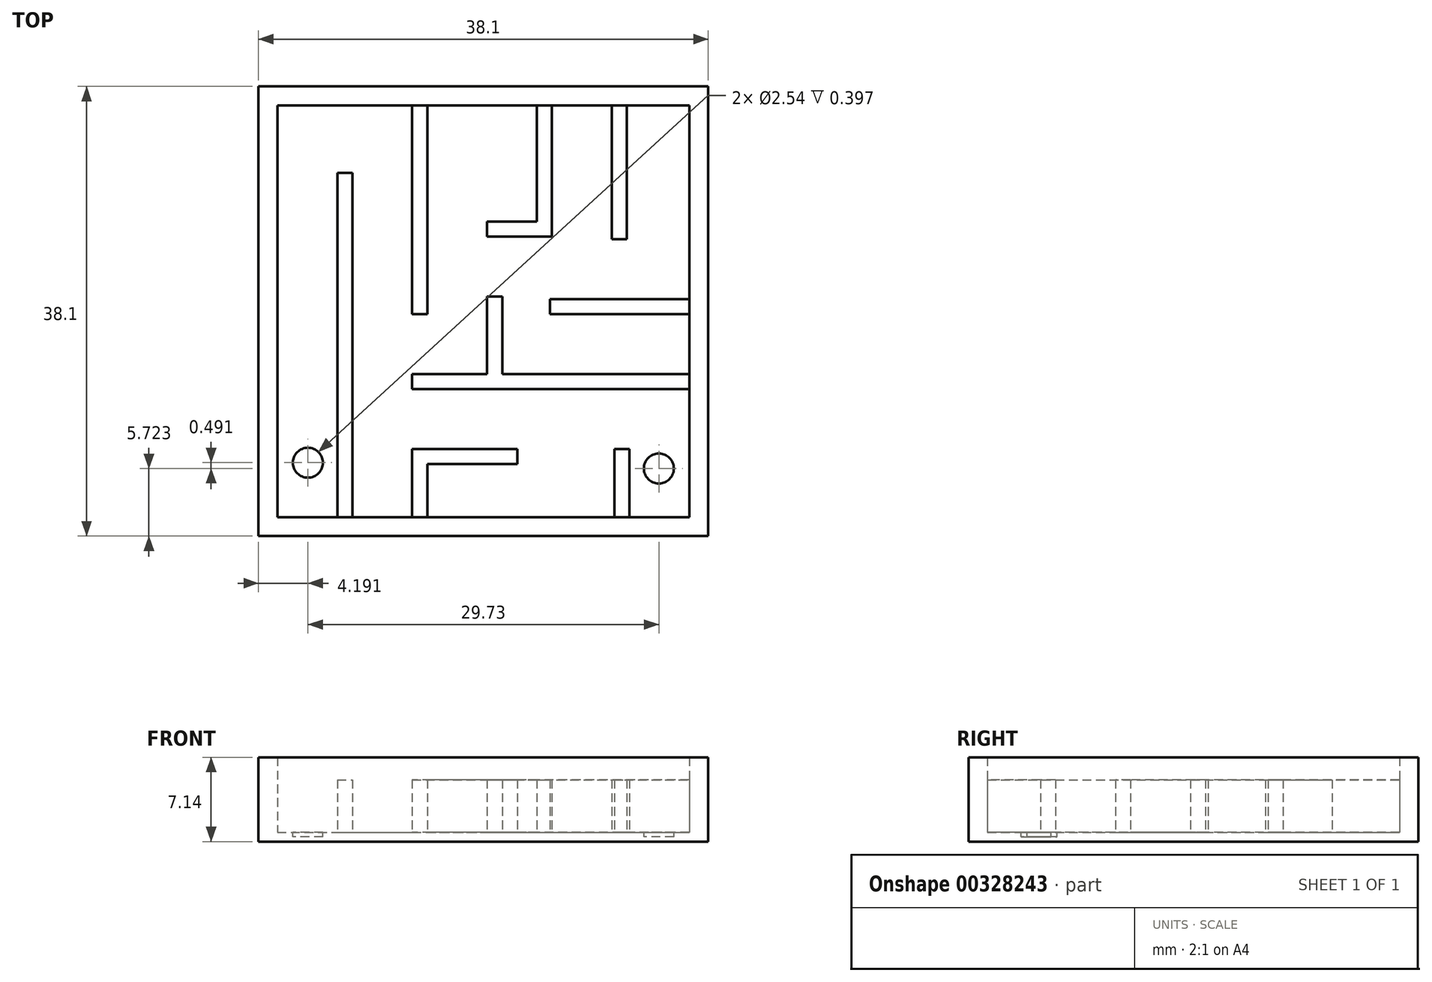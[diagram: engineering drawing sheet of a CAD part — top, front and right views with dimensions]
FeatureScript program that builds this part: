
annotation { "Feature Type Name" : "Feature", "Feature Type Description" : "" }
export const myFeature = defineFeature(function(context is Context, id is Id, definition is map)
    precondition{}
    {
        {
            var Q0;
            Q0=qCreatedBy(makeId("Top.planeOp"),FACE);
            var sketch = newSketch(context, id + "F0", { "sketchPlane" : qUnion([Q0])});
            skLineSegment(sketch, "E0.bottom", {"start": v(-16.83, 23.5) * mm, "end": v(21.27, 23.5) * mm});
            skLineSegment(sketch, "E0.top", {"start": v(-16.83, -14.6) * mm, "end": v(21.27, -14.6) * mm});
            skLineSegment(sketch, "E0.left", {"start": v(-16.83, 23.5) * mm, "end": v(-16.83, -14.6) * mm});
            skLineSegment(sketch, "E0.right", {"start": v(21.27, 23.5) * mm, "end": v(21.27, -14.6) * mm});
            skSolve(sketch);
        }
        {
            var Q0;
            Q0=makeQuery(id+"F0.imprint","IMPRINT",FACE,{"disambiguationData":[TD([[makeQuery(id+"F0.imprint","IMPRINT",EDGE,{"derivedFrom":sQuery(id+"F0.wireOp",EDGE,"E0.bottom")}),-1.0]])]});
            extrude(context, id + "F1", {"entities" : qUnion([Q0]), "depth" : 0.8 * mm});
        }
        {
            var Q0;
            Q0=makeQuery(id+"F1.opExtrude","CAP_FACE",FACE,{"disambiguationData":[OSD([sQuery(id+"F0.wireOp",EDGE,"E0.bottom"),sQuery(id+"F0.wireOp",EDGE,"E0.top"),sQuery(id+"F0.wireOp",EDGE,"E0.left"),sQuery(id+"F0.wireOp",EDGE,"E0.right")])],"isStart":false});
            var sketch = newSketch(context, id + "F2", { "sketchPlane" : qUnion([Q0])});
            skLineSegment(sketch, "E1.0", {"start": v(-15.23, 21.9) * mm, "end": v(19.67, 21.9) * mm});
            skLineSegment(sketch, "E1.1", {"start": v(-15.23, 21.9) * mm, "end": v(-15.23, -13) * mm});
            skLineSegment(sketch, "E1.2", {"start": v(-15.23, -13) * mm, "end": v(19.67, -13) * mm});
            skLineSegment(sketch, "E1.3", {"start": v(19.67, 21.9) * mm, "end": v(19.67, -13) * mm});
            skSolve(sketch);
        }
        {
            var Q0;
            Q0=makeQuery(id+"F2.imprint","IMPRINT",FACE,{"disambiguationData":[TD([[makeQuery(id+"F2.imprint","IMPRINT",EDGE,{"derivedFrom":sQuery(id+"F2.wireOp",EDGE,"E1.0")}),1.0]])]});
            extrude(context, id + "F3", {"entities" : qUnion([Q0]), "operationType" : NewBodyOperationType.ADD, "depth" : 6.35 * mm});
        }
        {
            var Q0;
            Q0=makeQuery(id+"F1.opExtrude","CAP_FACE",FACE,{"disambiguationData":[OSD([sQuery(id+"F0.wireOp",EDGE,"E0.bottom"),sQuery(id+"F0.wireOp",EDGE,"E0.top"),sQuery(id+"F0.wireOp",EDGE,"E0.left"),sQuery(id+"F0.wireOp",EDGE,"E0.right")])],"isStart":false});
            var sketch = newSketch(context, id + "F4", { "sketchPlane" : qUnion([Q0])});
            skLineSegment(sketch, "E2", {"start": v(-10.15, -13) * mm, "end": v(-10.15, 16.19) * mm});
            skLineSegment(sketch, "E3", {"start": v(-10.15, 16.19) * mm, "end": v(-8.88, 16.19) * mm});
            skLineSegment(sketch, "E4", {"start": v(-8.88, 16.19) * mm, "end": v(-8.88, -13) * mm});
            skLineSegment(sketch, "E5", {"start": v(-8.88, -13) * mm, "end": v(-10.15, -13) * mm});
            skLineSegment(sketch, "E6", {"start": v(-3.8, 21.9) * mm, "end": v(-3.8, 4.2) * mm});
            skLineSegment(sketch, "E7", {"start": v(-3.8, 4.2) * mm, "end": v(-2.53, 4.2) * mm});
            skLineSegment(sketch, "E8", {"start": v(-2.53, 4.2) * mm, "end": v(-2.53, 21.9) * mm});
            skLineSegment(sketch, "E9", {"start": v(-2.53, 21.9) * mm, "end": v(-3.8, 21.9) * mm});
            skLineSegment(sketch, "E10", {"start": v(-3.8, -0.88) * mm, "end": v(2.55, -0.88) * mm});
            skLineSegment(sketch, "E11", {"start": v(19.67, -0.88) * mm, "end": v(19.67, -2.15) * mm});
            skLineSegment(sketch, "E12", {"start": v(19.67, -2.15) * mm, "end": v(-3.8, -2.15) * mm});
            skLineSegment(sketch, "E13", {"start": v(-3.8, -2.15) * mm, "end": v(-3.8, -0.88) * mm});
            skLineSegment(sketch, "E14", {"start": v(19.67, 10.55) * mm, "end": v(19.67, 21.9) * mm});
            skLineSegment(sketch, "E15", {"start": v(19.67, 21.9) * mm, "end": v(2.55, 21.9) * mm});
            skLineSegment(sketch, "E16", {"start": v(2.55, -0.88) * mm, "end": v(2.55, 5.7) * mm});
            skLineSegment(sketch, "E17", {"start": v(2.55, 5.7) * mm, "end": v(3.82, 5.7) * mm});
            skLineSegment(sketch, "E18", {"start": v(3.82, 5.7) * mm, "end": v(3.82, -0.88) * mm});
            skLineSegment(sketch, "E19", {"start": v(-3.8, -13) * mm, "end": v(-3.8, -7.23) * mm});
            skLineSegment(sketch, "E20", {"start": v(-3.8, -7.23) * mm, "end": v(3.82, -7.23) * mm});
            skLineSegment(sketch, "E21", {"start": v(3.82, -7.23) * mm, "end": v(3.82, -7.23) * mm});
            skLineSegment(sketch, "E22", {"start": v(3.82, -7.23) * mm, "end": v(5.09, -7.23) * mm});
            skLineSegment(sketch, "E23", {"start": v(5.09, -7.23) * mm, "end": v(5.09, -8.5) * mm});
            skLineSegment(sketch, "E24", {"start": v(5.09, -8.5) * mm, "end": v(-2.53, -8.5) * mm});
            skLineSegment(sketch, "E25", {"start": v(-2.53, -8.5) * mm, "end": v(-2.53, -13) * mm});
            skLineSegment(sketch, "E26", {"start": v(-2.53, -13) * mm, "end": v(-3.8, -13) * mm});
            skLineSegment(sketch, "E27", {"start": v(19.67, -12.12) * mm, "end": v(19.67, -13) * mm});
            skLineSegment(sketch, "E28", {"start": v(19.67, -13) * mm, "end": v(13.32, -13) * mm});
            skLineSegment(sketch, "E29", {"start": v(-3.8, -8.5) * mm, "end": v(-3.8, -7.23) * mm});
            skLineSegment(sketch, "E30", {"start": v(14.59, -13) * mm, "end": v(19.67, -13) * mm});
            skPoint(sketch, "E31.start.orphan", {"position": v(-2.53, -7.23) * mm});
            skLineSegment(sketch, "E32.trimOffspring", {"start": v(3.82, -0.88) * mm, "end": v(19.67, -0.88) * mm});
            skLineSegment(sketch, "E33", {"start": v(6.77, 21.9) * mm, "end": v(6.77, 12.05) * mm});
            skLineSegment(sketch, "E34", {"start": v(6.77, 12.05) * mm, "end": v(2.55, 12.05) * mm});
            skLineSegment(sketch, "E35", {"start": v(2.55, 12.05) * mm, "end": v(2.55, 10.78) * mm});
            skLineSegment(sketch, "E36", {"start": v(2.55, 10.78) * mm, "end": v(8.04, 10.78) * mm});
            skLineSegment(sketch, "E37", {"start": v(8.04, 10.78) * mm, "end": v(8.04, 21.9) * mm});
            skLineSegment(sketch, "E38", {"start": v(8.04, 21.9) * mm, "end": v(6.77, 21.9) * mm});
            skLineSegment(sketch, "E39", {"start": v(19.67, 5.47) * mm, "end": v(7.87, 5.47) * mm});
            skLineSegment(sketch, "E40", {"start": v(7.87, 5.47) * mm, "end": v(7.87, 4.2) * mm});
            skLineSegment(sketch, "E41", {"start": v(7.87, 4.2) * mm, "end": v(19.67, 4.2) * mm});
            skPoint(sketch, "E41.endSnap0", {"position": v(19.67, 4.45) * mm});
            skLineSegment(sketch, "E42", {"start": v(19.67, 4.2) * mm, "end": v(19.67, 5.47) * mm});
            skLineSegment(sketch, "E43", {"start": v(13.12, 21.9) * mm, "end": v(13.12, 10.55) * mm});
            skLineSegment(sketch, "E44", {"start": v(13.12, 10.55) * mm, "end": v(14.39, 10.55) * mm});
            skLineSegment(sketch, "E45", {"start": v(14.39, 10.55) * mm, "end": v(14.39, 21.9) * mm});
            skLineSegment(sketch, "E46", {"start": v(14.39, 21.9) * mm, "end": v(13.12, 21.9) * mm});
            skPoint(sketch, "E47.end.orphan", {"position": v(6.77, 10.78) * mm});
            skPoint(sketch, "E48.start.orphan", {"position": v(13.32, -7.23) * mm});
            skLineSegment(sketch, "E49", {"start": v(13.32, -13) * mm, "end": v(13.32, -7.23) * mm});
            skLineSegment(sketch, "E50", {"start": v(13.32, -13) * mm, "end": v(14.59, -13) * mm});
            skLineSegment(sketch, "E51", {"start": v(14.59, -13) * mm, "end": v(14.59, -7.23) * mm});
            skLineSegment(sketch, "E52", {"start": v(14.59, -7.23) * mm, "end": v(13.32, -7.23) * mm});
            skSolve(sketch);
        }
        {
            var Q0;
            {var subQ16=sQuery(id+"F4.wireOp",EDGE,"E2");Q0=makeQuery(id+"F4.imprint","IMPRINT",FACE,{"disambiguationData":[TD([[makeQuery(id+"F4.imprint","IMPRINT",EDGE,{"derivedFrom":subQ16}),1.0]])]});}
            var sketch = newSketch(context, id + "F5", { "sketchPlane" : qUnion([Q0])});
            skLineSegment(sketch, "E53", {"start": v(-15.18, -12.8) * mm, "end": v(-10.1, -12.8) * mm});
            skCircle(sketch, "E54", {"center": v(-12.64, -8.39) * mm, "radius": 1.27 * mm});
            skPoint(sketch, "E54.centerSnap0", {"position": v(-12.64, -12.8) * mm});
            skLineSegment(sketch, "E55", {"start": v(14.55, -11.92) * mm, "end": v(19.63, -11.92) * mm});
            skCircle(sketch, "E56", {"center": v(17.1, -8.88) * mm, "radius": 1.27 * mm});
            skPoint(sketch, "E56.centerSnap0", {"position": v(17.1, -11.92) * mm});
            skSolve(sketch);
        }
        {
            var Q0;
            Q0=makeQuery(id+"F4.imprint","IMPRINT",FACE,{"disambiguationData":[TD([[makeQuery(id+"F4.imprint","IMPRINT",EDGE,{"derivedFrom":sQuery(id+"F4.wireOp",EDGE,"E6")}),1.0]])]});
            var Q1;
            Q1=makeQuery(id+"F4.imprint","IMPRINT",FACE,{"disambiguationData":[TD([[makeQuery(id+"F4.imprint","IMPRINT",EDGE,{"derivedFrom":sQuery(id+"F4.wireOp",EDGE,"E2")}),-1.0]])]});
            var Q2;
            Q2=makeQuery(id+"F4.imprint","IMPRINT",FACE,{"disambiguationData":[TD([[makeQuery(id+"F4.imprint","IMPRINT",EDGE,{"derivedFrom":sQuery(id+"F4.wireOp",EDGE,"E10")}),-1.0]])]});
            var Q3;
            Q3=makeQuery(id+"F4.imprint","IMPRINT",FACE,{"disambiguationData":[TD([[makeQuery(id+"F4.imprint","IMPRINT",EDGE,{"derivedFrom":sQuery(id+"F4.wireOp",EDGE,"E19")}),-1.0]])]});
            var Q4;
            Q4=makeQuery(id+"F4.imprint","IMPRINT",FACE,{"disambiguationData":[TD([[makeQuery(id+"F4.imprint","IMPRINT",EDGE,{"derivedFrom":sQuery(id+"F4.wireOp",EDGE,"VG6floot-Z6RI-uejr-kqyS-NIK7HqmhEphN")}),-1.0]])]});
            var Q5;
            Q5=makeQuery(id+"F4.imprint","IMPRINT",FACE,{"disambiguationData":[TD([[makeQuery(id+"F4.imprint","IMPRINT",EDGE,{"derivedFrom":sQuery(id+"F4.wireOp",EDGE,"E33")}),1.0]])]});
            var Q6;
            Q6=makeQuery(id+"F4.imprint","IMPRINT",FACE,{"disambiguationData":[TD([[makeQuery(id+"F4.imprint","IMPRINT",EDGE,{"derivedFrom":sQuery(id+"F4.wireOp",EDGE,"E39")}),1.0]])]});
            var Q7;
            Q7=makeQuery(id+"F4.imprint","IMPRINT",FACE,{"disambiguationData":[TD([[makeQuery(id+"F4.imprint","IMPRINT",EDGE,{"derivedFrom":sQuery(id+"F4.wireOp",EDGE,"E43")}),1.0]])]});
            var Q8;
            Q8=makeQuery(id+"F4.imprint","IMPRINT",FACE,{"disambiguationData":[TD([[makeQuery(id+"F4.imprint","IMPRINT",EDGE,{"derivedFrom":sQuery(id+"F4.wireOp",EDGE,"E49")}),-1.0]])]});
            extrude(context, id + "F6", {"entities" : qUnion([Q0, Q1, Q2, Q3, Q4, Q5, Q6, Q7, Q8]), "operationType" : NewBodyOperationType.ADD, "offsetDistance" : 25.4 * mm, "depth" : 4.44 * mm});
        }
        {
            var Q0;
            Q0=makeQuery(id+"F5.imprint","IMPRINT",FACE,{"disambiguationData":[TD([[makeQuery(id+"F5.imprint","IMPRINT",EDGE,{"derivedFrom":sQuery(id+"F5.wireOp",EDGE,"E56")}),1.0]])]});
            var Q1;
            Q1=makeQuery(id+"F5.imprint","IMPRINT",FACE,{"disambiguationData":[TD([[makeQuery(id+"F5.imprint","IMPRINT",EDGE,{"derivedFrom":sQuery(id+"F5.wireOp",EDGE,"E54")}),1.0]])]});
            extrude(context, id + "F7", {"entities" : qUnion([Q0, Q1]), "operationType" : NewBodyOperationType.REMOVE, "oppositeDirection" : true, "offsetDistance" : 25.4 * mm, "depth" : 0.4 * mm});
        }
    });
